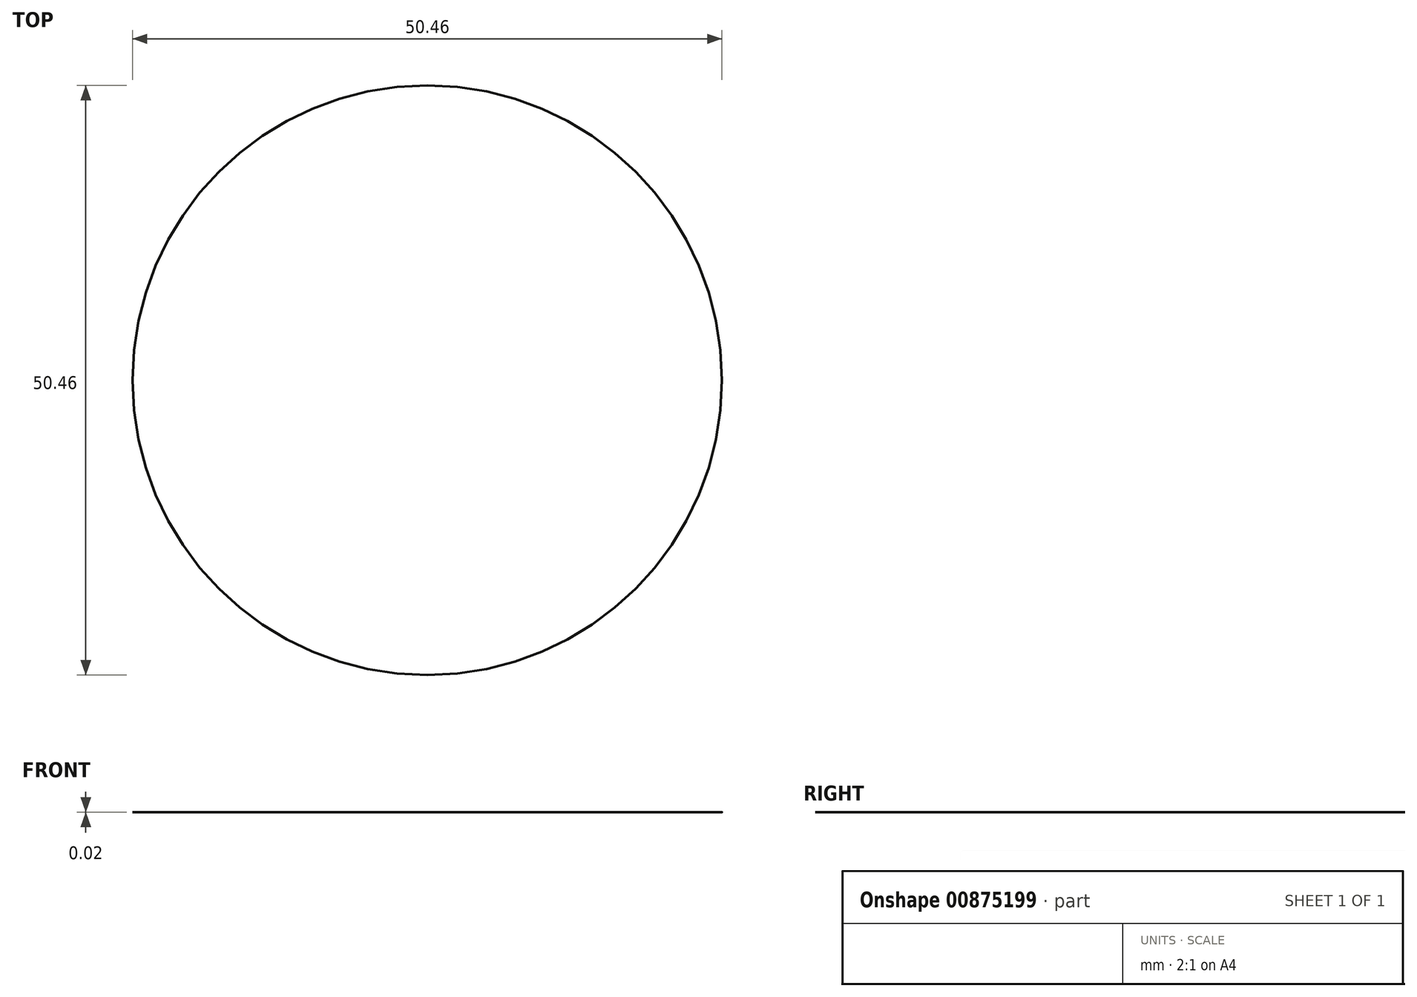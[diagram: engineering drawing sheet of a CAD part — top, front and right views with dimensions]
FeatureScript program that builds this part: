
annotation { "Feature Type Name" : "Feature", "Feature Type Description" : "" }
export const myFeature = defineFeature(function(context is Context, id is Id, definition is map)
    precondition{}
    {
        {
            var Q0;
            Q0=qCreatedBy(makeId("Top.planeOp"),FACE);
            var sketch = newSketch(context, id + "F0", { "sketchPlane" : qUnion([Q0])});
            skCircle(sketch, "E0", {"center": v(0, 0) * mm, "radius": 25.23 * mm});
            skSolve(sketch);
        }
        {
            var Q0;
            Q0=makeQuery(id+"F0.imprint","IMPRINT",FACE,{"disambiguationData":[TD([[makeQuery(id+"F0.imprint","IMPRINT",EDGE,{"derivedFrom":sQuery(id+"F0.wireOp",EDGE,"E0")}),1.0]])]});
            extrude(context, id + "F1", {"entities" : qUnion([Q0]), "depth" : 1 / 50.8 * mm, "offsetDistance" : 25.4 * mm});
        }
    });
